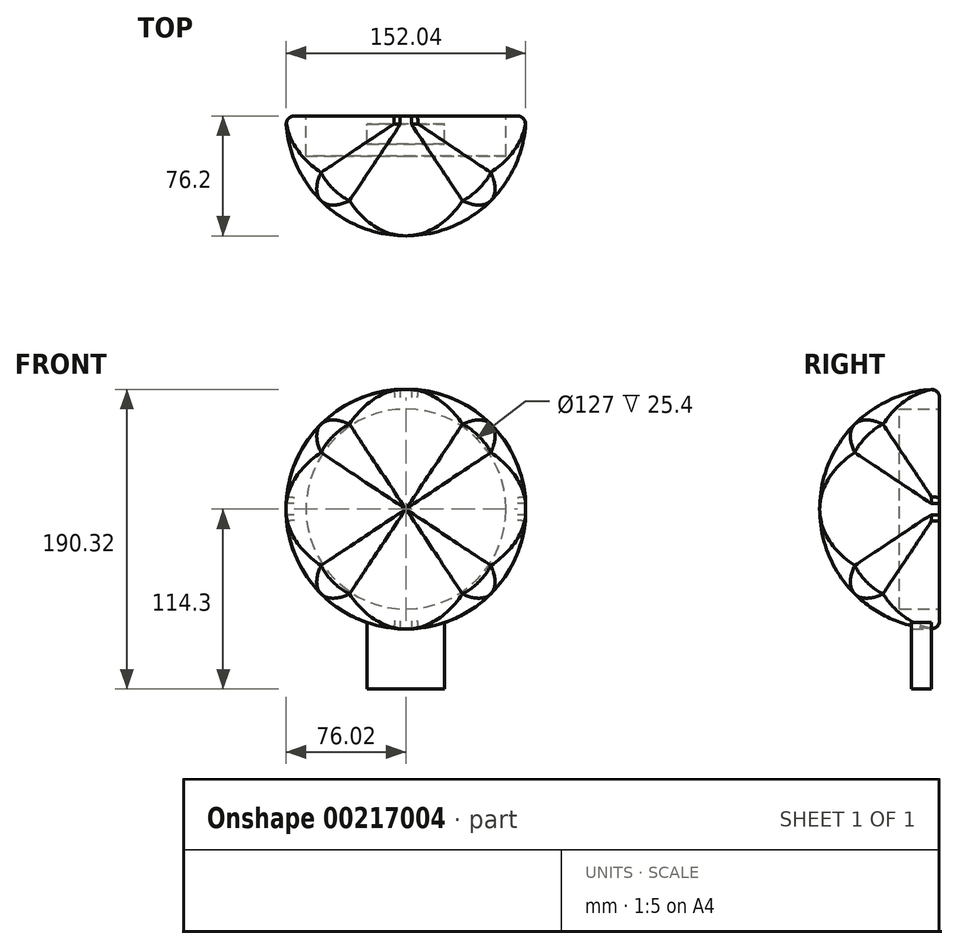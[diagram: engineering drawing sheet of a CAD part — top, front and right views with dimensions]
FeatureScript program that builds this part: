
annotation { "Feature Type Name" : "Feature", "Feature Type Description" : "" }
export const myFeature = defineFeature(function(context is Context, id is Id, definition is map)
    precondition{}
    {
        {
            var Q0;
            Q0=qCreatedBy(makeId("Front.planeOp"),FACE);
            var sketch = newSketch(context, id + "F0", { "sketchPlane" : qUnion([Q0])});
            skCircle(sketch, "E0", {"center": v(0, 0) * mm, "radius": 76.2 * mm});
            skCircle(sketch, "E1", {"center": v(0, 0) * mm, "radius": 63.5 * mm});
            skLineSegment(sketch, "E2", {"start": v(0, -114.3) * mm, "end": v(24.6, -114.3) * mm});
            skLineSegment(sketch, "E3", {"start": v(24.6, -114.3) * mm, "end": v(24.6, -72.12) * mm});
            skLineSegment(sketch, "E4.MirrorCS", {"start": v(0, -114.3) * mm, "end": v(-24.6, -114.3) * mm});
            skLineSegment(sketch, "E5.MirrorCS", {"start": v(-24.6, -114.3) * mm, "end": v(-24.6, -72.12) * mm});
            skPoint(sketch, "E6.start.orphan", {"position": v(0, -76.2) * mm});
            skSolve(sketch);
        }
        {
            var Q0;
            Q0=qCreatedBy(makeId("Top.planeOp"),FACE);
            var sketch = newSketch(context, id + "F1", { "sketchPlane" : qUnion([Q0])});
            skCircle(sketch, "E7", {"center": v(0, 0) * mm, "radius": 76.2 * mm});
            skLineSegment(sketch, "E8", {"start": v(76.2, 0) * mm, "end": v(84.96, -95.98) * mm});
            skLineSegment(sketch, "E9", {"start": v(84.96, -95.98) * mm, "end": v(-113.54, -82.25) * mm});
            skLineSegment(sketch, "E10", {"start": v(-113.54, -82.25) * mm, "end": v(-76.2, 0) * mm});
            skLineSegment(sketch, "E11", {"start": v(-76.2, 0) * mm, "end": v(-145.63, 41.79) * mm});
            skSolve(sketch);
        }
        {
            var Q0;
            Q0=qCreatedBy(makeId("Right.planeOp"),FACE);
            var sketch = newSketch(context, id + "F2", { "sketchPlane" : qUnion([Q0])});
            skCircle(sketch, "E12", {"center": v(0, 0) * mm, "radius": 76.2 * mm});
            skLineSegment(sketch, "E13", {"start": v(0, 76.2) * mm, "end": v(-82.17, 76.2) * mm});
            skLineSegment(sketch, "E14", {"start": v(-82.17, 76.2) * mm, "end": v(-76.42, 0) * mm});
            skLineSegment(sketch, "E15", {"start": v(-76.42, 0) * mm, "end": v(-90.11, -87.22) * mm});
            skLineSegment(sketch, "E16", {"start": v(-90.11, -87.22) * mm, "end": v(0, -76.72) * mm});
            skLineSegment(sketch, "E17", {"start": v(0, -76.72) * mm, "end": v(0, 76.2) * mm});
            skSolve(sketch);
        }
        {
            var Q0;
            Q0=makeQuery(id+"F0.imprint","IMPRINT",FACE,{"disambiguationData":[TD([[makeQuery(id+"F0.imprint","IMPRINT",EDGE,{"derivedFrom":sQuery(id+"F0.wireOp",EDGE,"E0")}),1.0]])]});
            var Q1;
            Q1=makeQuery(id+"F0.imprint","IMPRINT",FACE,{"disambiguationData":[TD([[makeQuery(id+"F0.imprint","IMPRINT",EDGE,{"derivedFrom":sQuery(id+"F0.wireOp",EDGE,"E1")}),1.0]])]});
            extrude(context, id + "F3", {"entities" : qUnion([Q0, Q1]), "depth" : 76.2 * mm});
        }
        {
            var Q0;
            {var subQ0=sQuery(id+"F2.wireOp",EDGE,"E13");Q0=makeQuery(id+"F2.imprint","IMPRINT",FACE,{"disambiguationData":[TD([[makeQuery(id+"F2.imprint","IMPRINT",EDGE,{"derivedFrom":subQ0}),1.0]])]});}
            extrude(context, id + "F4", {"entities" : qUnion([Q0]), "operationType" : NewBodyOperationType.REMOVE, "oppositeDirection" : true, "depth" : 177.8 * mm, "symmetric" : true});
        }
        {
            var Q0;
            {var subQ0=sQuery(id+"F1.wireOp",EDGE,"E8");Q0=makeQuery(id+"F1.imprint","IMPRINT",FACE,{"disambiguationData":[TD([[makeQuery(id+"F1.imprint","IMPRINT",EDGE,{"derivedFrom":subQ0}),-1.0]])]});}
            extrude(context, id + "F5", {"entities" : qUnion([Q0]), "operationType" : NewBodyOperationType.REMOVE, "oppositeDirection" : true, "depth" : 152.4 * mm, "symmetric" : true});
        }
        {
            var Q0;
            Q0=makeQuery(id+"F5.boolean.opBoolean","INTERSECT",EDGE,{"disambiguationData":[OD(1.0)],"derivedFrom":[makeQuery(id+"F4.boolean.opBoolean","SPLIT",FACE,{"disambiguationData":[OD(1.0)],"derivedFrom":makeQuery(id+"F3.opExtrude","SWEPT_FACE",FACE,{"disambiguationData":[OSD([sQuery(id+"F0.wireOp",EDGE,"E0")])]})}),makeQuery(id+"F5.opExtrude","SWEPT_FACE",FACE,{"disambiguationData":[OSD([sQuery(id+"F1.wireOp",EDGE,"E7")])]})]});
            var Q1;
            Q1=makeQuery(id+"F5.boolean.opBoolean","SPLIT",EDGE,{"disambiguationData":[OD(1.0)],"derivedFrom":makeQuery(id+"F4.boolean.opBoolean","INTERSECT",EDGE,{"disambiguationData":[OD(1.0)],"derivedFrom":[makeQuery(id+"F3.opExtrude","SWEPT_FACE",FACE,{"disambiguationData":[OSD([sQuery(id+"F0.wireOp",EDGE,"E0")])]}),makeQuery(id+"F4.opExtrude","SWEPT_FACE",FACE,{"disambiguationData":[OSD([sQuery(id+"F2.wireOp",EDGE,"E12")])]})]})});
            var Q2;
            Q2=makeQuery(id+"F5.boolean.opBoolean","INTERSECT",EDGE,{"disambiguationData":[OD(3.0)],"derivedFrom":[makeQuery(id+"F4.boolean.opBoolean","COPY",FACE,{"derivedFrom":makeQuery(id+"F4.opExtrude","SWEPT_FACE",FACE,{"disambiguationData":[OSD([sQuery(id+"F2.wireOp",EDGE,"E12")])]})}),makeQuery(id+"F5.opExtrude","SWEPT_FACE",FACE,{"disambiguationData":[OSD([sQuery(id+"F1.wireOp",EDGE,"E7")])]})]});
            var Q3;
            Q3=makeQuery(id+"F5.boolean.opBoolean","INTERSECT",EDGE,{"disambiguationData":[OD(0.0)],"derivedFrom":[makeQuery(id+"F4.boolean.opBoolean","SPLIT",FACE,{"disambiguationData":[OD(1.0)],"derivedFrom":makeQuery(id+"F3.opExtrude","SWEPT_FACE",FACE,{"disambiguationData":[OSD([sQuery(id+"F0.wireOp",EDGE,"E0")])]})}),makeQuery(id+"F5.opExtrude","SWEPT_FACE",FACE,{"disambiguationData":[OSD([sQuery(id+"F1.wireOp",EDGE,"E7")])]})]});
            var Q4;
            Q4=makeQuery(id+"F5.boolean.opBoolean","INTERSECT",EDGE,{"disambiguationData":[OD(2.0)],"derivedFrom":[makeQuery(id+"F4.boolean.opBoolean","COPY",FACE,{"derivedFrom":makeQuery(id+"F4.opExtrude","SWEPT_FACE",FACE,{"disambiguationData":[OSD([sQuery(id+"F2.wireOp",EDGE,"E12")])]})}),makeQuery(id+"F5.opExtrude","SWEPT_FACE",FACE,{"disambiguationData":[OSD([sQuery(id+"F1.wireOp",EDGE,"E7")])]})]});
            var Q5;
            Q5=makeQuery(id+"F5.boolean.opBoolean","INTERSECT",EDGE,{"disambiguationData":[OD(0.0)],"derivedFrom":[makeQuery(id+"F4.boolean.opBoolean","COPY",FACE,{"derivedFrom":makeQuery(id+"F4.opExtrude","SWEPT_FACE",FACE,{"disambiguationData":[OSD([sQuery(id+"F2.wireOp",EDGE,"E12")])]})}),makeQuery(id+"F5.opExtrude","SWEPT_FACE",FACE,{"disambiguationData":[OSD([sQuery(id+"F1.wireOp",EDGE,"E7")])]})]});
            var Q6;
            Q6=makeQuery(id+"F5.boolean.opBoolean","INTERSECT",EDGE,{"disambiguationData":[OD(1.0)],"derivedFrom":[makeQuery(id+"F4.boolean.opBoolean","COPY",FACE,{"derivedFrom":makeQuery(id+"F4.opExtrude","SWEPT_FACE",FACE,{"disambiguationData":[OSD([sQuery(id+"F2.wireOp",EDGE,"E12")])]})}),makeQuery(id+"F5.opExtrude","SWEPT_FACE",FACE,{"disambiguationData":[OSD([sQuery(id+"F1.wireOp",EDGE,"E7")])]})]});
            var Q7;
            Q7=makeQuery(id+"F5.boolean.opBoolean","SPLIT",EDGE,{"disambiguationData":[OD(1.0)],"derivedFrom":makeQuery(id+"F4.boolean.opBoolean","INTERSECT",EDGE,{"disambiguationData":[OD(0.0)],"derivedFrom":[makeQuery(id+"F3.opExtrude","SWEPT_FACE",FACE,{"disambiguationData":[OSD([sQuery(id+"F0.wireOp",EDGE,"E0")])]}),makeQuery(id+"F4.opExtrude","SWEPT_FACE",FACE,{"disambiguationData":[OSD([sQuery(id+"F2.wireOp",EDGE,"E12")])]})]})});
            var Q8;
            Q8=makeQuery(id+"F5.boolean.opBoolean","INTERSECT",EDGE,{"disambiguationData":[OD(1.0)],"derivedFrom":[makeQuery(id+"F4.boolean.opBoolean","SPLIT",FACE,{"disambiguationData":[OD(0.0)],"derivedFrom":makeQuery(id+"F3.opExtrude","SWEPT_FACE",FACE,{"disambiguationData":[OSD([sQuery(id+"F0.wireOp",EDGE,"E0")])]})}),makeQuery(id+"F5.opExtrude","SWEPT_FACE",FACE,{"disambiguationData":[OSD([sQuery(id+"F1.wireOp",EDGE,"E7")])]})]});
            var Q9;
            Q9=makeQuery(id+"F5.boolean.opBoolean","INTERSECT",EDGE,{"disambiguationData":[OD(0.0)],"derivedFrom":[makeQuery(id+"F4.boolean.opBoolean","SPLIT",FACE,{"disambiguationData":[OD(0.0)],"derivedFrom":makeQuery(id+"F3.opExtrude","SWEPT_FACE",FACE,{"disambiguationData":[OSD([sQuery(id+"F0.wireOp",EDGE,"E0")])]})}),makeQuery(id+"F5.opExtrude","SWEPT_FACE",FACE,{"disambiguationData":[OSD([sQuery(id+"F1.wireOp",EDGE,"E7")])]})]});
            var Q10;
            Q10=makeQuery(id+"F5.boolean.opBoolean","SPLIT",EDGE,{"disambiguationData":[OD(0.0)],"derivedFrom":makeQuery(id+"F4.boolean.opBoolean","INTERSECT",EDGE,{"disambiguationData":[OD(0.0)],"derivedFrom":[makeQuery(id+"F3.opExtrude","SWEPT_FACE",FACE,{"disambiguationData":[OSD([sQuery(id+"F0.wireOp",EDGE,"E0")])]}),makeQuery(id+"F4.opExtrude","SWEPT_FACE",FACE,{"disambiguationData":[OSD([sQuery(id+"F2.wireOp",EDGE,"E12")])]})]})});
            var Q11;
            Q11=makeQuery(id+"F5.boolean.opBoolean","SPLIT",EDGE,{"disambiguationData":[OD(0.0)],"derivedFrom":makeQuery(id+"F4.boolean.opBoolean","INTERSECT",EDGE,{"disambiguationData":[OD(1.0)],"derivedFrom":[makeQuery(id+"F3.opExtrude","SWEPT_FACE",FACE,{"disambiguationData":[OSD([sQuery(id+"F0.wireOp",EDGE,"E0")])]}),makeQuery(id+"F4.opExtrude","SWEPT_FACE",FACE,{"disambiguationData":[OSD([sQuery(id+"F2.wireOp",EDGE,"E12")])]})]})});
            fillet(context, id + "F6", {"entities" : qUnion([Q0, Q1, Q2, Q3, Q4, Q5, Q6, Q7, Q8, Q9, Q10, Q11]), "radius" : 25.4 * mm, "tangentPropagation" : true, "allowEdgeOverflow" : false});
        }
        {
            var Q0;
            Q0=makeQuery(id+"F0.imprint","IMPRINT",FACE,{"disambiguationData":[TD([[makeQuery(id+"F0.imprint","IMPRINT",EDGE,{"derivedFrom":sQuery(id+"F0.wireOp",EDGE,"E1")}),1.0]])]});
            extrude(context, id + "F7", {"entities" : qUnion([Q0]), "operationType" : NewBodyOperationType.REMOVE, "depth" : 25.4 * mm});
        }
        {
            var Q0;
            Q0=makeQuery(id+"F7.boolean.opBoolean","COPY",EDGE,{"derivedFrom":makeQuery(id+"F7.opExtrude","CAP_EDGE",EDGE,{"disambiguationData":[OSD([sQuery(id+"F0.wireOp",EDGE,"E1")])],"isStart":true})});
            var Q1;
            Q1=makeQuery(id+"F5.boolean.opBoolean","SPLIT",EDGE,{"disambiguationData":[OD(0.0)],"derivedFrom":makeQuery(id+"F4.boolean.opBoolean","SPLIT",EDGE,{"disambiguationData":[OD(0.0)],"derivedFrom":makeQuery(id+"F3.opExtrude","CAP_EDGE",EDGE,{"disambiguationData":[OSD([sQuery(id+"F0.wireOp",EDGE,"E0")])],"isStart":true})})});
            var Q2;
            Q2=makeQuery(id+"F5.boolean.opBoolean","SPLIT",EDGE,{"disambiguationData":[OD(1.0)],"derivedFrom":makeQuery(id+"F4.boolean.opBoolean","SPLIT",EDGE,{"disambiguationData":[OD(0.0)],"derivedFrom":makeQuery(id+"F3.opExtrude","CAP_EDGE",EDGE,{"disambiguationData":[OSD([sQuery(id+"F0.wireOp",EDGE,"E0")])],"isStart":true})})});
            var Q3;
            Q3=makeQuery(id+"F5.boolean.opBoolean","SPLIT",EDGE,{"disambiguationData":[OD(1.0)],"derivedFrom":makeQuery(id+"F4.boolean.opBoolean","SPLIT",EDGE,{"disambiguationData":[OD(1.0)],"derivedFrom":makeQuery(id+"F3.opExtrude","CAP_EDGE",EDGE,{"disambiguationData":[OSD([sQuery(id+"F0.wireOp",EDGE,"E0")])],"isStart":true})})});
            var Q4;
            Q4=makeQuery(id+"F5.boolean.opBoolean","SPLIT",EDGE,{"disambiguationData":[OD(0.0)],"derivedFrom":makeQuery(id+"F4.boolean.opBoolean","SPLIT",EDGE,{"disambiguationData":[OD(1.0)],"derivedFrom":makeQuery(id+"F3.opExtrude","CAP_EDGE",EDGE,{"disambiguationData":[OSD([sQuery(id+"F0.wireOp",EDGE,"E0")])],"isStart":true})})});
            fillet(context, id + "F8", {"entities" : qUnion([Q0, Q1, Q2, Q3, Q4]), "radius" : 5.08 * mm, "tangentPropagation" : true, "allowEdgeOverflow" : false});
        }
        {
            var Q0;
            Q0=makeQuery(id+"F0.imprint","IMPRINT",FACE,{"disambiguationData":[TD([[makeQuery(id+"F0.imprint","IMPRINT",EDGE,{"derivedFrom":sQuery(id+"F0.wireOp",EDGE,"E2")}),1.0]])]});
            extrude(context, id + "F9", {"entities" : qUnion([Q0]), "operationType" : NewBodyOperationType.ADD, "depth" : 17.78 * mm});
        }
        {
            var Q0;
            Q0=makeQuery(id+"F9.opExtrude","CAP_FACE",FACE,{"disambiguationData":[OSD([sQuery(id+"F0.wireOp",EDGE,"E0"),sQuery(id+"F0.wireOp",EDGE,"E2"),sQuery(id+"F0.wireOp",EDGE,"E3"),sQuery(id+"F0.wireOp",EDGE,"E4.MirrorCS"),sQuery(id+"F0.wireOp",EDGE,"E5.MirrorCS")])],"isStart":true});
            extrude(context, id + "F10", {"entities" : qUnion([Q0]), "operationType" : NewBodyOperationType.REMOVE, "oppositeDirection" : true, "depth" : 5.08 * mm});
        }
    });
